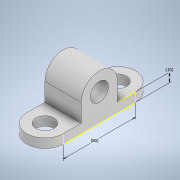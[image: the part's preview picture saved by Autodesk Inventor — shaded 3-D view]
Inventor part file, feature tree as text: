
AUTODESK INVENTOR PART (.ipt)
format: ipt  version: 2022 (Build 260153000, 153)  size: 137,216 bytes
history: native  units: mm
features: sketch x3, extrude x2
ambient origin geometry x8: Origin, YZ Plane, XZ Plane, XY Plane, X Axis, Y Axis, Z Axis, Center Point
bodies: Solid1 (feature_tree)
feature tree (5):
  extrude  "Extrusion1"  Depth=20.0mm
  extrude  "Extrusion2"  Depth=40.0mm
  sketch  "Sketch3"  dims[d12=20.0mm d13=40.0mm d14=0.0mm d15=80.0mm d16=10.0mm]
  sketch  "Sketch1"  dims[d3=20.0mm d6=20.0mm]
  sketch  "Sketch2"  dims[d8=10.0mm d9=0.0mm d11=40.0mm]
